# Revit family: CFO
name_source: partatom
category: Air Terminals
revit_build: Autodesk Revit MEP 2012 (Build: 20110309_2315(x64)
units: mm (PartAtom-declared; Revit-internal decimal feet)

## types (4) — shared parameters

## per-type parameters (varying)
| type | A Cuello | A1 | B Plato | B1 | B2 | C | Cuello | Manufacturer | Material | Max Flow | Min Flow | Minima presión estática | Minima velocidad de cuello | Máxima presión estática | Máxima velocidad de cuello | Radio A | Tipo | URL |
| CFO-E-C-06-24 | 6" | 5" | 23 3/4" | 18 3/4" | 22 3/4" | 19 3/4" |  |  |  | 0 CFM | 0 CFM | 0.00 in-wg | 0 FPM | 0.00 in-wg | 0 FPM | 3" |  |  |
| CFO-E-R-06-24 | 6" | 5" | 23 3/4" | 18 3/4" | 22 3/4" | 19 3/4" |  | INNES |  | 0 CFM | 0 CFM | 0.00 in-wg | 0 FPM | 0.00 in-wg | 0 FPM | 3" |  | http://www.innes.com.mx |
| CFO-D-R-06-12 | 6" | 5" | 11 3/4" | 6 3/4" | 10 3/4" | 7 3/4" | Redondo | INNES | Aluminio/Acero | 315 CFM | 80 CFM | 0.02 in-wg | 400 FPM | 0.30 in-wg | 2000 FPM | 3" | Doblado | http://www.innes.com.mx |
| CFO-D-R-08-12 | 8" | 7" | 11 3/4" | 6 3/4" | 10 3/4" | 7 3/4" | Redondo | INNES | Aluminio/Acero | 0 CFM | 0 CFM | 0.00 in-wg | 0 FPM | 0.00 in-wg | 0 FPM | 4" | Doblado | http://www.innes.com.mx |

## geometry (parser evidence)
native form markers: Sweep x1
no freeform markers — native parametric forms only
